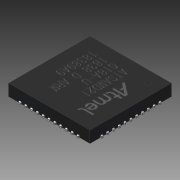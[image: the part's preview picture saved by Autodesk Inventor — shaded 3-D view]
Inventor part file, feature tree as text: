
AUTODESK INVENTOR PART (.ipt)
format: ipt  version: 2016 (Build 200138000, 138)  size: 3,632,128 bytes
history: native  units: mm
features: other x3, extrude x2, sketch x2, projected_geometry x1, chamfer x1
ambient origin geometry x8: Origin, YZ Plane, XZ Plane, XY Plane, X Axis, Y Axis, Z Axis, Center Point
bodies: Body1 (feature_tree)
feature tree (9):
  other  "Blocks"
  extrude  "Extrusion4"  Depth=4.081232mm
  extrude  "Extrusion5"  Depth=1.0mm
  sketch  "Sketch10"  dims[d7=10.0mm d8=0.0mm d9=4.081232mm]
  projected_geometry  "Projected Loop1"
  sketch  "Sketch11"  dims[d10=1.0mm d11=1.0mm d12=0.4mm d13=5.0mm d14=3.5mm d15=0.05mm d16=0.0mm]
  other  "Atmel Logo"
  chamfer  "Chamfer1"  Distance=0.4mm
  other  "Atmel Logo:1"
